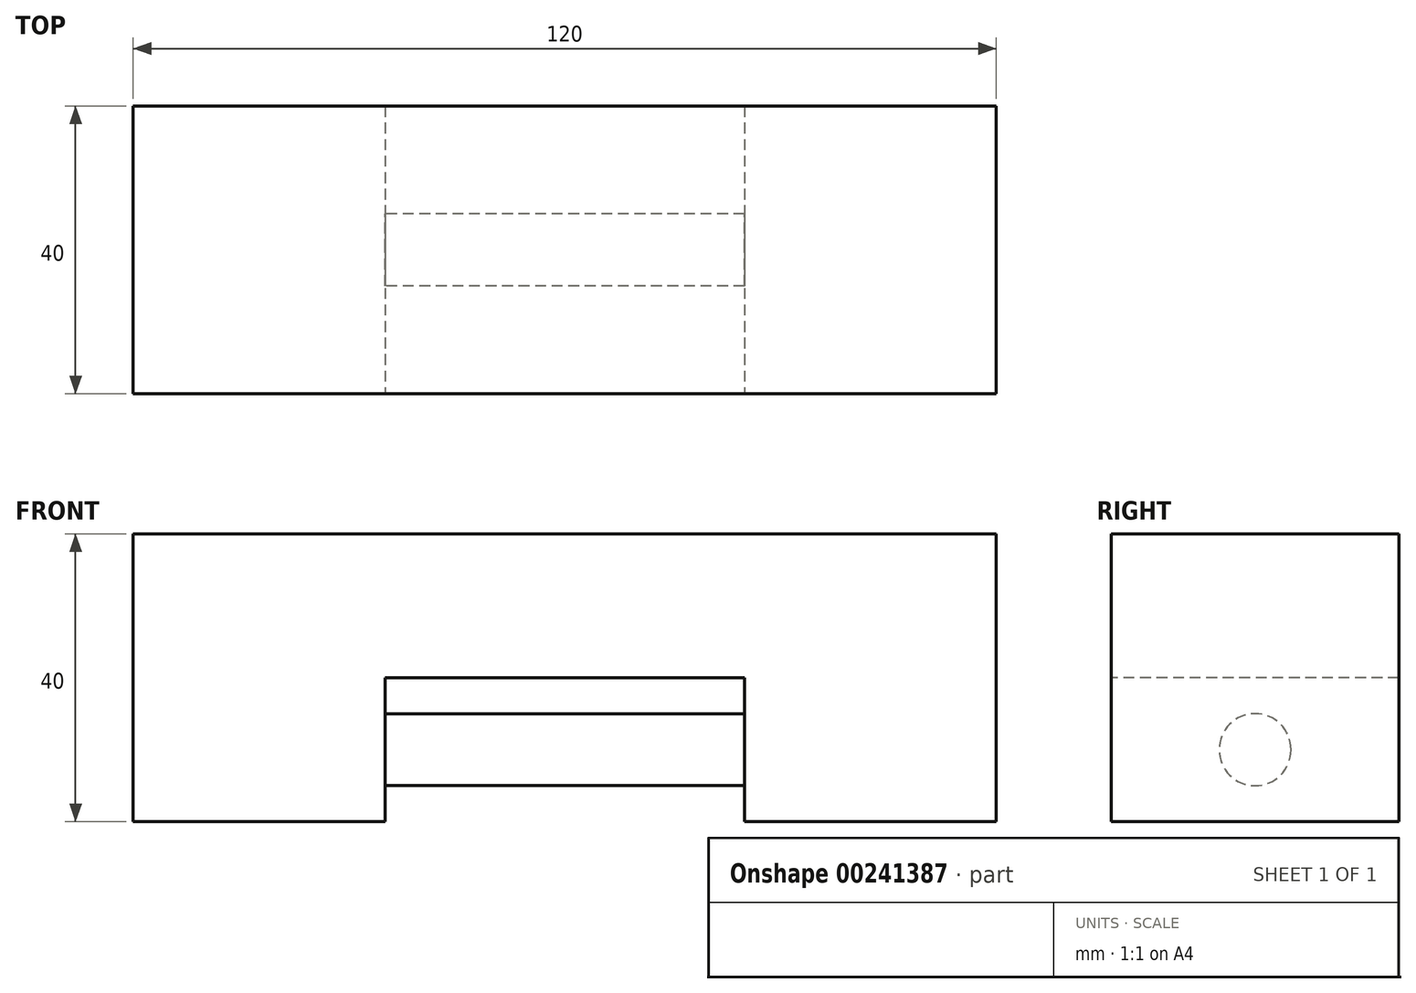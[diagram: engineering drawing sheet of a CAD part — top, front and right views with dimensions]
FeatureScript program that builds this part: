
annotation { "Feature Type Name" : "Feature", "Feature Type Description" : "" }
export const myFeature = defineFeature(function(context is Context, id is Id, definition is map)
    precondition{}
    {
        {
            var Q0;
            Q0=qCreatedBy(makeId("Right.planeOp"),FACE);
            var sketch = newSketch(context, id + "F0", { "sketchPlane" : qUnion([Q0])});
            skLineSegment(sketch, "E0.bottom", {"start": v(-20, 20) * mm, "end": v(20, 20) * mm});
            skLineSegment(sketch, "E0.top", {"start": v(-20, -20) * mm, "end": v(20, -20) * mm});
            skLineSegment(sketch, "E0.left", {"start": v(-20, 20) * mm, "end": v(-20, -20) * mm});
            skLineSegment(sketch, "E0.right", {"start": v(20, 20) * mm, "end": v(20, -20) * mm});
            skPoint(sketch, "E0.middle", {"position": v(0, 0) * mm});
            skSolve(sketch);
        }
        {
            var Q0;
            Q0 = qSketchRegion(id + "F0", true);
            extrude(context, id + "F1", {"entities" : qUnion([Q0]), "endBound" : BoundingType.SYMMETRIC, "depth" : 120 * mm});
        }
        {
            var Q0;
            Q0=makeQuery(id+"F1.opExtrude","SWEPT_FACE",FACE,{"disambiguationData":[OSD([sQuery(id+"F0.wireOp",EDGE,"E0.left")])]});
            var sketch = newSketch(context, id + "F2", { "sketchPlane" : qUnion([Q0])});
            skLineSegment(sketch, "E1.bottom", {"start": v(-25, -20) * mm, "end": v(25, -20) * mm});
            skLineSegment(sketch, "E1.top", {"start": v(-25, 0) * mm, "end": v(25, 0) * mm});
            skLineSegment(sketch, "E1.left", {"start": v(-25, -20) * mm, "end": v(-25, 0) * mm});
            skLineSegment(sketch, "E1.right", {"start": v(25, -20) * mm, "end": v(25, 0) * mm});
            skSolve(sketch);
        }
        {
            var Q0;
            Q0 = qSketchRegion(id + "F2", true);
            extrude(context, id + "F3", {"entities" : qUnion([Q0]), "operationType" : NewBodyOperationType.REMOVE, "endBound" : BoundingType.THROUGH_ALL, "oppositeDirection" : true, "depth" : 25 * mm});
        }
        {
            var Q0;
            Q0=qCreatedBy(makeId("Right.planeOp"),FACE);
            var sketch = newSketch(context, id + "F4", { "sketchPlane" : qUnion([Q0])});
            skCircle(sketch, "E2", {"center": v(0, -10) * mm, "radius": 5 * mm});
            skSolve(sketch);
        }
        {
            var Q0;
            Q0 = qSketchRegion(id + "F4", true);
            extrude(context, id + "F5", {"entities" : qUnion([Q0]), "operationType" : NewBodyOperationType.ADD, "endBound" : BoundingType.SYMMETRIC, "depth" : 50 * mm});
        }
    });
